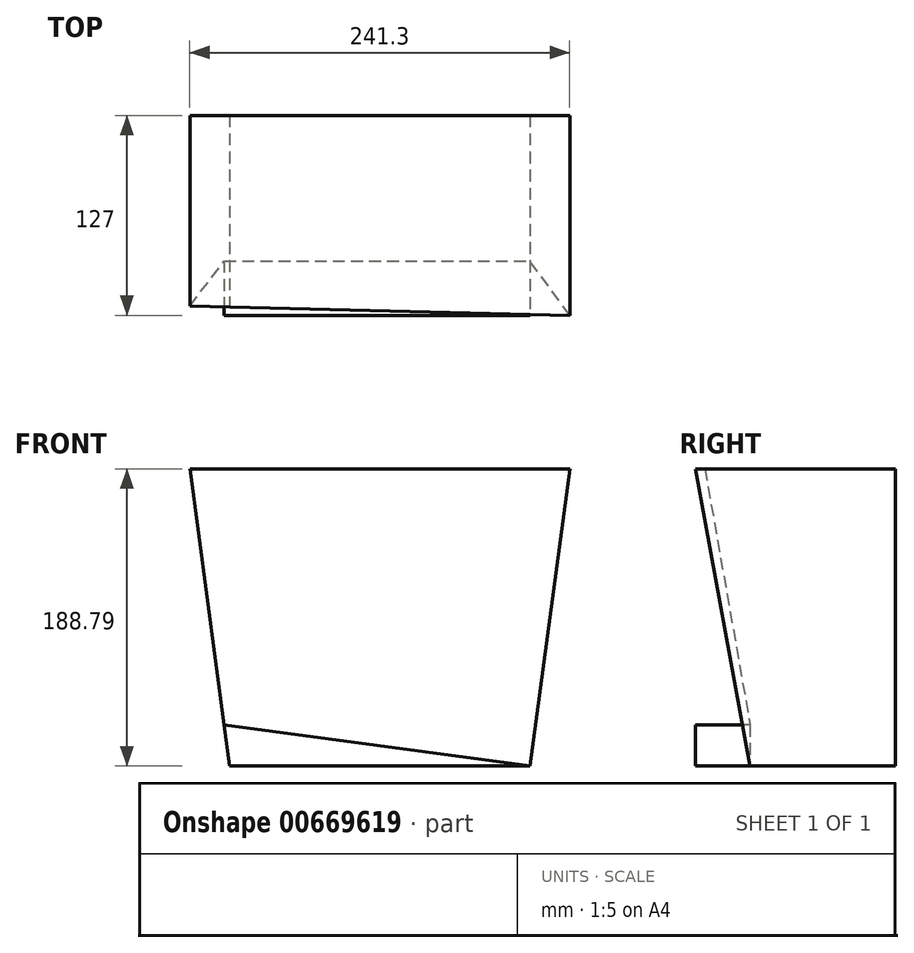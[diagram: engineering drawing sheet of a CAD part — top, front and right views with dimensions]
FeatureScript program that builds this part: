
annotation { "Feature Type Name" : "Feature", "Feature Type Description" : "" }
export const myFeature = defineFeature(function(context is Context, id is Id, definition is map)
    precondition{}
    {
        {
            var Q0;
            Q0=qCreatedBy(makeId("Front.planeOp"),FACE);
            var sketch = newSketch(context, id + "F0", { "sketchPlane" : qUnion([Q0])});
            skLineSegment(sketch, "E0", {"start": v(-86.28, 76.16) * mm, "end": v(155.02, 76.16) * mm});
            skLineSegment(sketch, "E1", {"start": v(155.02, 76.16) * mm, "end": v(129.62, -112.63) * mm});
            skLineSegment(sketch, "E2", {"start": v(129.62, -112.63) * mm, "end": v(-60.88, -112.63) * mm});
            skLineSegment(sketch, "E3", {"start": v(-60.88, -112.63) * mm, "end": v(-86.28, 76.16) * mm});
            skSolve(sketch);
        }
        {
            var Q0;
            Q0=makeQuery(id+"F0.imprint","IMPRINT",FACE,{"disambiguationData":[TD([[makeQuery(id+"F0.imprint","IMPRINT",EDGE,{"derivedFrom":sQuery(id+"F0.wireOp",EDGE,"E0")}),-1.0]])]});
            extrude(context, id + "F1", {"entities" : qUnion([Q0]), "oppositeDirection" : true, "depth" : 127 * mm, "offsetDistance" : 25.4 * mm});
        }
        {
            var Q0;
            Q0=makeQuery(id+"F1.opExtrude","SWEPT_FACE",FACE,{"disambiguationData":[OSD([sQuery(id+"F0.wireOp",EDGE,"E1")])]});
            var sketch = newSketch(context, id + "F2", { "sketchPlane" : qUnion([Q0])});
            skLineSegment(sketch, "E4", {"start": v(0, 96.15) * mm, "end": v(34.57, -94.35) * mm});
            skLineSegment(sketch, "E5", {"start": v(34.57, -94.35) * mm, "end": v(0, -94.35) * mm});
            skLineSegment(sketch, "E6", {"start": v(0, -94.35) * mm, "end": v(0, 96.15) * mm});
            skSolve(sketch);
        }
        {
            var Q0;
            Q0=makeQuery(id+"F2.imprint","IMPRINT",FACE,{"disambiguationData":[TD([[makeQuery(id+"F2.imprint","IMPRINT",EDGE,{"derivedFrom":sQuery(id+"F2.wireOp",EDGE,"E4")}),-1.0]])]});
            extrude(context, id + "F3", {"entities" : qUnion([Q0]), "operationType" : NewBodyOperationType.REMOVE, "oppositeDirection" : true, "depth" : 241.3 * mm, "offsetDistance" : 25.4 * mm});
        }
    });
